# Revit family: PRESTO ECO XT-UE PS
name_source: partatom
category: Aparatos sanitarios
revit_build: Autodesk Revit 2015 (Build: 20140223_1515(x64)
units: mm (PartAtom-declared; Revit-internal decimal feet)

## types (1)
- 11636
    Accionamiento = Por pulsador
    CAUDAL = 5 L/Min
    CIERRE = Automático en 5 seg.
    Comentarios de tipo = ◦Cabeza intercambiable que comprende todo el mecanismo del grifo
◦Cuerpo y pulsador en latón cromado, piezas interiores en materiales resistentes a la corrosión y a las incrustaciones calcáreas
◦Tornillos en acero inoxidable.
    Conexión AC = Sí
    Conexión AF = Sí
    Código de montaje = C1030220
    Descripción = Grifo temporizado ecológico de un agua para instalación empotrada con cuerpo de latón cromado.
    ENTRADA = Macho y Hembra 1/2"
    Elevación por defecto = 1219 mm
    Fabricante = PRESTO IBÉRICA
    Imagen de tipo = <Ninguno>
    Material = LATON CROMADO
    Modelo = PRESTO ECO XT UE PS
    PESO BRUTO = 0.481  Kg
    REFERENCIA = 11636
    TIPO DE AGUA = Fria
    Teléfono = (+34) 915 782 575
    URL = http://www.prestoiberica.com

## geometry (parser evidence)
native form markers: Blend x3
no freeform markers — native parametric forms only
